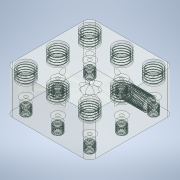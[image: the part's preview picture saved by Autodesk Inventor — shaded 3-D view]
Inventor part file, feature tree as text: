
AUTODESK INVENTOR PART (.ipt)
format: ipt  version: 2020 (Build 240168000, 168)  size: 8,176,128 bytes
history: native  units: mm
features: sketch x48, thread x18, revolve x17, helix x17, extrude x14, plane x3
ambient origin geometry x8: Origin, YZ Plane, XZ Plane, XY Plane, X Axis, Y Axis, Z Axis, Center Point
bodies: Solid1 (feature_tree), Solid20 (feature_tree), Solid21 (feature_tree), Solid22 (feature_tree), Solid23 (feature_tree), Solid24 (feature_tree), Solid25 (feature_tree), Solid26 (feature_tree), Solid27 (feature_tree), Solid36 (feature_tree), Solid37 (feature_tree), Solid38 (feature_tree), Solid39 (feature_tree), Solid40 (feature_tree), Solid41 (feature_tree), Solid42 (feature_tree), Solid43 (feature_tree), Solid45 (feature_tree)
feature tree (117):
  extrude  "Extrusion1"  Depth=13.157mm
  extrude  "Extrusion2"  Depth=26.0mm
  extrude  "Extrusion3"  Depth=10.0mm TaperAngle=0.0deg
  extrude  "Extrusion4"  Depth=26.0mm
  thread  "Thread25"  [1 undecoded]
  thread  "Thread26"  [1 undecoded]
  thread  "Thread27"  [1 undecoded]
  thread  "Thread28"  [1 undecoded]
  thread  "Thread29"  [1 undecoded]
  thread  "Thread30"  [1 undecoded]
  thread  "Thread31"  [1 undecoded]
  thread  "Thread32"  [1 undecoded]
  extrude  "Extrusion9"  Depth=19.0mm
  extrude  "Extrusion10"  Depth=5.0mm
  extrude  "Extrusion11"  TaperAngle=45.0deg  [1 undecoded]
  plane  "Work Plane2"
  extrude  "Extrusion12"  Depth=70.0mm TaperAngle=0.0deg
  extrude  "Extrusion14"  Depth=35.0mm TaperAngle=0.0deg
  thread  "Thread33"  [1 undecoded]
  thread  "Thread34"  [1 undecoded]
  thread  "Thread35"  [1 undecoded]
  thread  "Thread36"  [1 undecoded]
  thread  "Thread37"  [1 undecoded]
  thread  "Thread38"  [1 undecoded]
  thread  "Thread39"  [1 undecoded]
  thread  "Thread40"  [1 undecoded]
  thread  "Thread41"  [1 undecoded]
  revolve  "Revolution19"  [1 undecoded]
  helix  "Coil19"  [1 undecoded]
  revolve  "Revolution20"  [1 undecoded]
  helix  "Coil20"  [1 undecoded]
  revolve  "Revolution21"  [1 undecoded]
  helix  "Coil21"  [1 undecoded]
  revolve  "Revolution22"  [1 undecoded]
  helix  "Coil22"  [1 undecoded]
  revolve  "Revolution23"  [1 undecoded]
  helix  "Coil23"  [1 undecoded]
  revolve  "Revolution24"  [1 undecoded]
  helix  "Coil24"  [1 undecoded]
  revolve  "Revolution25"  [1 undecoded]
  helix  "Coil25"  [1 undecoded]
  revolve  "Revolution26"  [1 undecoded]
  helix  "Coil26"  [1 undecoded]
  plane  "Work Plane3"
  extrude  "Extrusion16"  TaperAngle=0.0deg  [1 undecoded]
  extrude  "Extrusion18"  Depth=10.0mm
  revolve  "Revolution35"  [1 undecoded]
  helix  "Coil35"  [1 undecoded]
  revolve  "Revolution36"  [1 undecoded]
  helix  "Coil36"  [1 undecoded]
  revolve  "Revolution37"  [1 undecoded]
  helix  "Coil37"  [1 undecoded]
  revolve  "Revolution38"  [1 undecoded]
  helix  "Coil38"  [1 undecoded]
  revolve  "Revolution39"  [1 undecoded]
  helix  "Coil39"  [1 undecoded]
  revolve  "Revolution40"  [1 undecoded]
  helix  "Coil40"  [1 undecoded]
  revolve  "Revolution41"  [1 undecoded]
  helix  "Coil41"  [1 undecoded]
  revolve  "Revolution42"  [1 undecoded]
  helix  "Coil42"  [1 undecoded]
  extrude  "Extrusion19"  TaperAngle=0.0deg  [1 undecoded]
  extrude  "Extrusion20"  Depth=10.0mm
  thread  "Thread42"  [1 undecoded]
  extrude  "Extrusion21"  Depth=9.599311mm
  revolve  "Revolution44"  [1 undecoded]
  helix  "Coil44"  [1 undecoded]
  sketch  "Sketch1"  dims[d0=68.0mm d1=68.0mm d2=5.0mm d3=34.0mm d4=0.0mm d5=13.157mm]
  sketch  "Sketch2"  dims[d7=26.0mm d8=26.0mm]
  sketch  "Sketch5"  dims[d9=30.0mm d11=26.0mm d12=30.0mm d14=26.0mm d17=10.0mm d18=0.0mm]
  sketch  "Sketch6"  dims[d20=30.0mm d22=30.0mm d23=9.0mm d24=26.0mm d25=26.0mm d26=26.0mm d27=26.0mm d28=12.0mm d29=0.0mm]
  sketch  "Sketch12"  dims[d31=30.0mm d33=30.0mm d34=7.25mm d35=26.0mm d36=26.0mm d37=26.0mm d38=26.0mm d39=13.5mm d40=0.0mm d107=7.0mm d108=2.0mm d109=7.0mm d110=2.0mm d111=7.0mm d112=2.0mm d113=7.0mm d114=2.0mm d115=7.0mm d116=2.0mm d117=7.0mm d118=2.0mm d119=7.0mm d120=2.0mm d121=7.0mm d122=2.0mm d123=10.9mm]
  sketch  "Sketch13"  dims[d124=19.0mm d125=0.0mm d126=5.0mm]
  sketch  "Sketch14"  dims[d127=50.0mm d128=0.0mm d129=5.0mm]
  plane  "Work Plane1"
  sketch  "Sketch15"  dims[d130=50.0mm d131=0.0mm d132=45.0deg d133=90.0deg]
  sketch  "Sketch17"  dims[d134=5.0mm d135=70.0mm d136=0.0mm]
  sketch  "Sketch54"  dims[d140=5.0mm d141=35.0mm d142=0.0mm d143=6.0mm d144=0.0mm d145=6.0mm d146=0.0mm d147=6.0mm d148=0.0mm d149=6.0mm d150=0.0mm d151=6.0mm d152=0.0mm d153=6.0mm d154=0.0mm d155=6.0mm d156=0.0mm d157=6.0mm d158=0.0mm d159=6.0mm d160=0.0mm]
  sketch  "Sketch55"  dims[d168=9.599311mm d186=9.599311mm d204=9.599311mm]
  sketch  "Sketch56"  dims[d222=9.599311mm d240=9.599311mm d258=9.599311mm]
  sketch  "Sketch57"  dims[d276=9.599311mm d294=9.599311mm d312=9.599311mm]
  sketch  "Sketch58"  dims[d330=9.599311mm d348=9.599311mm d366=9.599311mm]
  sketch  "Sketch59"  dims[d384=9.599311mm d402=9.599311mm d420=9.599311mm]
  sketch  "Sketch60"  dims[d438=9.599311mm d456=9.599311mm d474=9.599311mm]
  sketch  "Sketch61"  dims[d485=9.599311mm d486=0.145218mm d487=0.145218mm d490=0.907143mm d492=9.599311mm]
  sketch  "Sketch62"  dims[d494=0.0mm]
  sketch  "Sketch63"  dims[d495=0.90805mm d496=7.814286mm d497=10.0mm d498=0.0mm d499=0.0mm d500=0.0mm d501=0.0mm d502=0.0mm d503=9.599311mm d504=0.145218mm d505=0.145218mm d508=0.907143mm]
  sketch  "Sketch64"  dims[d510=9.599311mm d512=0.0mm]
  sketch  "Sketch65"  dims[d513=0.90805mm d514=7.814286mm d515=10.0mm d516=0.0mm d517=0.0mm d518=0.0mm d519=0.0mm d520=0.0mm d521=9.599311mm d522=0.145218mm d523=0.145218mm]
  sketch  "Sketch66"  dims[d526=0.907143mm d528=9.599311mm d530=0.0mm]
  sketch  "Sketch67"  dims[d531=0.90805mm d532=7.814286mm d533=10.0mm d534=0.0mm d535=0.0mm d536=0.0mm d537=0.0mm d538=0.0mm d539=9.599311mm d540=0.145218mm d541=0.145218mm d544=0.907143mm]
  sketch  "Sketch68"  dims[d546=9.599311mm d548=0.0mm]
  sketch  "Sketch69"  dims[d549=0.90805mm d550=7.814286mm d551=10.0mm d552=0.0mm d553=0.0mm d554=0.0mm d555=0.0mm d556=0.0mm d557=9.599311mm d558=0.145218mm d559=0.145218mm]
  sketch  "Sketch87"  dims[d562=0.907143mm d564=9.599311mm d566=0.0mm]
  sketch  "Sketch89"  dims[d567=0.90805mm d568=7.814286mm d569=10.0mm d570=0.0mm d571=0.0mm d572=0.0mm d573=0.0mm d574=0.0mm d575=9.599311mm d576=0.145218mm d577=0.145218mm d580=0.907143mm]
  sketch  "Sketch90"  dims[d582=9.599311mm d584=0.0mm]
  sketch  "Sketch91"  dims[d585=0.90805mm d586=7.814286mm d587=10.0mm d588=0.0mm d589=0.0mm d590=0.0mm d591=0.0mm d592=0.0mm d593=9.599311mm d594=0.145218mm d595=0.145218mm]
  sketch  "Sketch92"  dims[d598=0.907143mm d600=9.599311mm d602=0.0mm]
  sketch  "Sketch93"  dims[d603=0.90805mm d604=7.814286mm d605=10.0mm d606=0.0mm d607=0.0mm d608=0.0mm d609=0.0mm d610=0.0mm d611=9.599311mm d612=0.145218mm d613=0.145218mm d616=0.907143mm]
  sketch  "Sketch94"  dims[d618=9.599311mm d620=0.0mm]
  sketch  "Sketch95"  dims[d621=0.90805mm d622=7.814286mm d623=10.0mm d624=0.0mm d625=0.0mm d626=0.0mm d627=0.0mm d628=0.0mm d636=9.599311mm d654=9.599311mm]
  sketch  "Sketch96"  dims[d672=9.599311mm d690=9.599311mm]
  sketch  "Sketch97"  dims[d708=9.599311mm d726=9.599311mm d744=9.599311mm]
  sketch  "Sketch98"  dims[d762=9.599311mm]
  sketch  "Sketch99"  dims[d784=-8.0mm]
  sketch  "Sketch100"  dims[d785=3.0mm]
  sketch  "Sketch101"  dims[d786=10.0mm]
  sketch  "Sketch102"  dims[d787=30.0mm d789=26.0mm d790=30.0mm d792=26.0mm]
  sketch  "Sketch103"  dims[d795=4.0mm d796=0.0mm]
  sketch  "Sketch104"  dims[d808=13.2mm]
  sketch  "Sketch105"  dims[d809=30.0mm d811=26.0mm d812=30.0mm d814=26.0mm]
  sketch  "Sketch106"  dims[d817=2.0mm d818=0.0mm]
  sketch  "Sketch107"  dims[d819=9.599311mm d820=0.290436mm d821=0.290436mm]
  sketch  "Sketch108"  dims[d824=1.814286mm]
  sketch  "Sketch111"  dims[d826=9.599311mm]
  sketch  "Sketch112"  dims[d828=0.0mm d829=1.8161mm d830=10.628571mm d831=10.0mm d832=0.0mm d833=0.0mm d834=0.0mm d835=0.0mm d836=0.0mm d837=9.599311mm d838=0.290436mm d839=0.290436mm d842=1.814286mm d844=9.599311mm d846=0.0mm d847=1.8161mm d848=10.628571mm d849=10.0mm d850=0.0mm d851=0.0mm d852=0.0mm d853=0.0mm d854=0.0mm d855=9.599311mm d856=0.290436mm d857=0.290436mm d860=1.814286mm d862=9.599311mm d864=0.0mm d865=1.8161mm d866=10.628571mm d867=10.0mm d868=0.0mm d869=0.0mm d870=0.0mm d871=0.0mm d872=0.0mm d873=9.599311mm d874=0.290436mm d875=0.290436mm d878=1.814286mm d880=9.599311mm d882=0.0mm d883=1.8161mm d884=10.628571mm d885=10.0mm d886=0.0mm d887=0.0mm d888=0.0mm d889=0.0mm d890=0.0mm d891=9.599311mm d892=0.290436mm d893=0.290436mm d896=1.814286mm d898=9.599311mm d900=0.0mm d901=1.8161mm d902=10.628571mm d903=10.0mm d904=0.0mm d905=0.0mm d906=0.0mm d907=0.0mm d908=0.0mm d909=9.599311mm d910=0.290436mm d911=0.290436mm d914=1.814286mm d916=9.599311mm d918=0.0mm d919=1.8161mm d920=10.628571mm d921=10.0mm d922=0.0mm d923=0.0mm d924=0.0mm d925=0.0mm d926=0.0mm d927=9.599311mm d928=0.290436mm d929=0.290436mm d932=1.814286mm d934=9.599311mm d936=0.0mm d937=1.8161mm d938=10.628571mm d939=10.0mm d940=0.0mm d941=0.0mm d942=0.0mm d943=0.0mm d944=0.0mm d945=9.599311mm d946=0.290436mm d947=0.290436mm d950=1.814286mm d952=9.599311mm d954=0.0mm d955=1.8161mm d956=10.628571mm d957=10.0mm d958=0.0mm d959=0.0mm d960=0.0mm d961=0.0mm d962=0.0mm d964=10.0mm d965=10.87mm d966=26.0mm d967=0.0mm d968=19.0mm d969=7.0mm d970=20.0mm d971=0.0mm d972=17.0mm d973=0.0mm d974=10.0mm d975=0.0mm d983=9.599311mm d994=9.599311mm d995=0.145218mm d996=0.145218mm d999=0.907143mm d1001=9.599311mm d1003=0.0mm d1004=0.90805mm d1005=18.814286mm d1006=10.0mm d1007=0.0mm d1008=0.0mm d1009=0.0mm d1010=0.0mm d1011=0.0mm]
note: 55 required parameter values undecoded (feature->parameter linkage not recoverable at this tier; creation-order binding heuristic only, values carry confidence <= 0.55)